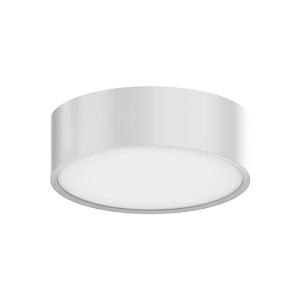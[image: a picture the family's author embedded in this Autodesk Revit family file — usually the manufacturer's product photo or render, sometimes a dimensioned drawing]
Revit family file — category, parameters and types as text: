
# Revit family: ledceilinglu-e_rd142-24w-840-wh_540001296600
name_source: partatom
category: Leuchten
revit_build: Autodesk Revit 2016 (Build: 20190508_0715(x64)
units: mm (PartAtom-declared; Revit-internal decimal feet)

## family parameters
Basisbauteil = Fläche
Beim Laden mit Abzugskörper schneiden = Nein
Bemaßung runder Anschluss = Durchmesser verwenden
Gemeinsam genutzt = Nein
Lichtquelle = Nein
Raumberechnungspunkt = Nein
Teiletyp = Normal

## types (1)
- LEDCeilingLu-E Rd142-24W-840-WH (1 x LED, 2160 lm)
    Approval mark = CE
    Beschreibung = Stylish and compact ceiling luminaire. Clean “twist-and-lock” mounting system. High quality full metal body. Low height of only 46mm. Suitable for ceiling and wall mounting.
    CIE Flux Codes = 48 79 96 100 100
    Control Gear = Electronic ballast
    Height = 100 mm  [stored 0.328084 ft]
    Hersteller = OPPLE
    Lamp Light Flux = 2160 lm
    Lamp count = 1
    Lampe = 1 x LED
    Length = 100 mm  [stored 0.328084 ft]
    Luminous efficacy = 90 lm/W
    ModVariant = Nein
    Modell = 540001296600
    Mounting Place = Wall, Ceiling
    Mounting Type = Surface mounted
    Number of Poles = 1
    OnlyDefault = Ja
    Power Factor = 1
    Product Name = LEDCeilingLu-E Rd142-24W-840-WH
    Product group = Ceiling Light Luna
    ProductGroupID = 305
    Protection Class = Protection class II
    Protection Degree = IP 20
    RLX_Detail_Level = 1
    RlxData = <blob elided: 125149 chars, md5=dd10e0ae>
    Scheinlast = 24 VA
    Socket = socket
    Standby Power = 0 W
    System Light Flux = 2160 lm
    System Power = 24 W
    Typenbild = luna_wh_rd142.jpg
    Typenkommentare = Product without accessories
    URL = http://relux.com
    VarID = ---
    Voltage = 230 V
    Voltage Range = 220-240 V
    Vorgabe-Ansicht = 1800 mm
    Weight = 0.00 kg
    Width = 100 mm  [stored 0.328084 ft]

note: [stored X ft] marks values corroborated as IEEE doubles in the binary element streams (Revit-internal decimal feet)

## geometry (parser evidence)
native form markers: Blend x4, Sweep x12
no freeform markers — native parametric forms only
